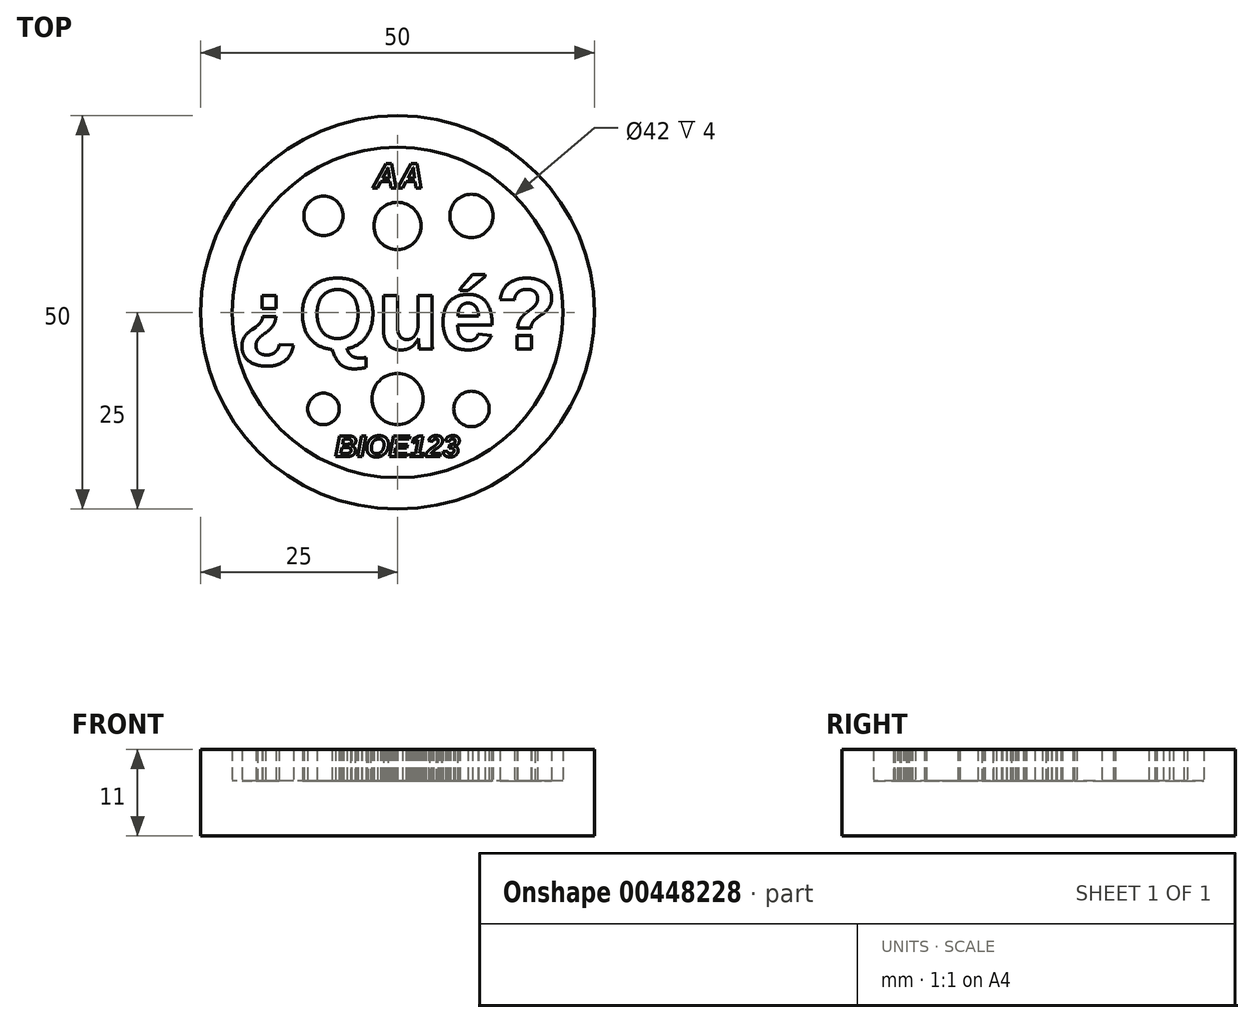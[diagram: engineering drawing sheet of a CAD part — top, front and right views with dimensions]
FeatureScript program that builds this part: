
annotation { "Feature Type Name" : "Feature", "Feature Type Description" : "" }
export const myFeature = defineFeature(function(context is Context, id is Id, definition is map)
    precondition{}
    {
        {
            var Q0;
            Q0=qCreatedBy(makeId("Top.planeOp"),FACE);
            var sketch = newSketch(context, id + "F0", { "sketchPlane" : qUnion([Q0])});
            skCircle(sketch, "E0", {"center": v(0, 0) * mm, "radius": 25 * mm});
            skCircle(sketch, "E1", {"center": v(0, 0) * mm, "radius": 21 * mm});
            skSolve(sketch);
        }
        {
            var Q0;
            Q0=makeQuery(id+"F0.imprint","IMPRINT",FACE,{"disambiguationData":[TD([[makeQuery(id+"F0.imprint","IMPRINT",EDGE,{"derivedFrom":sQuery(id+"F0.wireOp",EDGE,"E0")}),1.0]])]});
            extrude(context, id + "F1", {"entities" : qUnion([Q0]), "depth" : 11 * mm});
        }
        {
            var Q0;
            Q0=qCreatedBy(makeId("Top.planeOp"),FACE);
            var sketch = newSketch(context, id + "F2", { "sketchPlane" : qUnion([Q0])});
            skCircle(sketch, "E2", {"center": v(0, 0) * mm, "radius": 21 * mm});
            skSolve(sketch);
        }
        {
            var Q0;
            Q0 = qSketchRegion(id + "F2", true);
            extrude(context, id + "F3", {"entities" : qUnion([Q0]), "operationType" : NewBodyOperationType.ADD, "depth" : 7 * mm});
        }
        {
            var Q0;
            Q0=qCreatedBy(makeId("Top.planeOp"),FACE);
            var sketch = newSketch(context, id + "F4", { "sketchPlane" : qUnion([Q0])});
            skText(sketch, "E3", { "text": "¿Qué?", "fontName": "Arimo-Bold.ttf"});
            skCircle(sketch, "E4", {"center": v(-9.4, 12.26) * mm, "radius": 2.5 * mm});
            skCircle(sketch, "E5", {"center": v(9.4, 12.26) * mm, "radius": 2.75 * mm});
            skCircle(sketch, "E6", {"center": v(-9.4, -12.26) * mm, "radius": 2 * mm});
            skCircle(sketch, "E7", {"center": v(9.4, -12.26) * mm, "radius": 2.25 * mm});
            skCircle(sketch, "E8", {"center": v(0, 10.99) * mm, "radius": 3 * mm});
            skCircle(sketch, "E9", {"center": v(0, -10.99) * mm, "radius": 3.25 * mm});
            skText(sketch, "E10", { "text": "BIOE123", "fontName": "Arimo-BoldItalic.ttf"});
            skText(sketch, "E11", { "text": "AA", "fontName": "Arimo-BoldItalic.ttf"});
            const initialGuessF4  = {"E3": [-0.02048, -0.00464, 1, 0, 0.00928], "E10": [-0.00792, -0.01833, 1, 0, 0.00277], "E11": [-0.0031, 0.01582, 1, 0, 0.0032]};
            skSetInitialGuess(sketch, initialGuessF4);
            skSolve(sketch);
        }
        {
            var Q0;
            Q0 = qSketchRegion(id + "F4", true);
            extrude(context, id + "F5", {"entities" : qUnion([Q0]), "operationType" : NewBodyOperationType.ADD, "depth" : 11 * mm});
        }
    });
